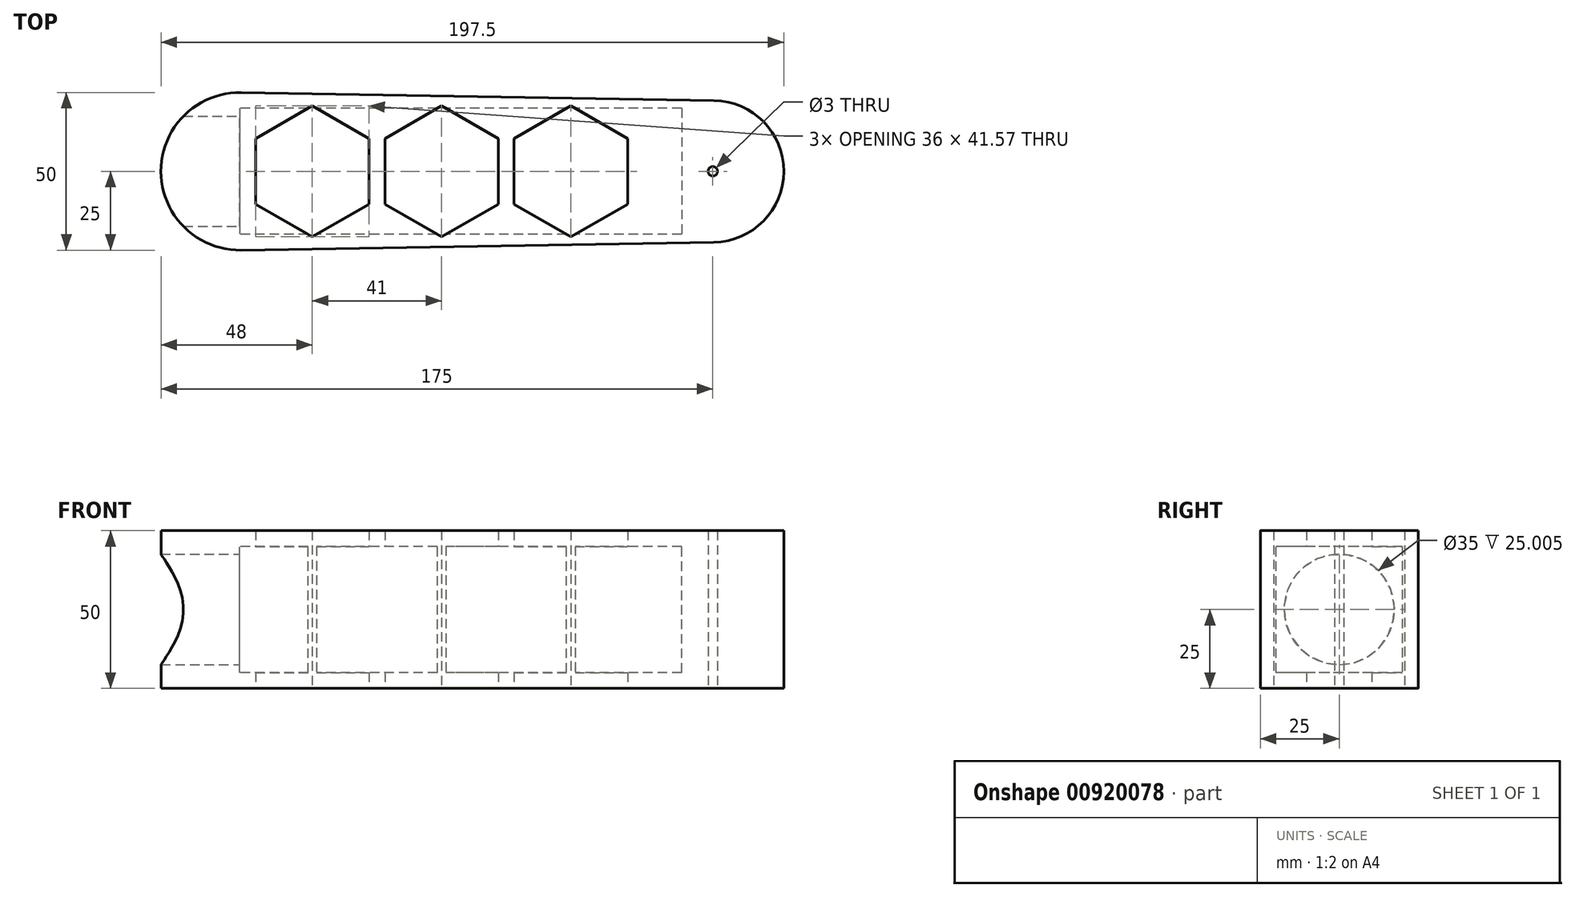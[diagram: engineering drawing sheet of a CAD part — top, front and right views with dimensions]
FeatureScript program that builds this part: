
annotation { "Feature Type Name" : "Feature", "Feature Type Description" : "" }
export const myFeature = defineFeature(function(context is Context, id is Id, definition is map)
    precondition{}
    {
        {
            var Q0;
            Q0=qCreatedBy(makeId("Top.planeOp"),FACE);
            var sketch = newSketch(context, id + "F0", { "sketchPlane" : qUnion([Q0])});
            skCircle(sketch, "E0", {"center": v(150, 0) * mm, "radius": 1.5 * mm});
            skLineSegment(sketch, "E1", {"start": v(0, 0) * mm, "end": v(150, 0) * mm, "construction": true});
            skArc(sketch, "E2", {"start": v(0.42, 25) * mm, "mid": v(-25, 0) * mm, "end": v(0.42, -25) * mm});
            skLineSegment(sketch, "E3", {"start": v(0.42, 25) * mm, "end": v(150.37, 22.5) * mm});
            skLineSegment(sketch, "E4", {"start": v(150.37, -22.5) * mm, "end": v(0.42, -25) * mm});
            skArc(sketch, "E5", {"start": v(150.37, 22.5) * mm, "mid": v(127.5, 0) * mm, "end": v(150.37, -22.5) * mm, "construction": true});
            skArc(sketch, "E6", {"start": v(150.37, -22.5) * mm, "mid": v(172.5, 0) * mm, "end": v(150.37, 22.5) * mm});
            skSolve(sketch);
        }
        {
            var Q0;
            Q0=makeQuery(id+"F0.imprint","IMPRINT",FACE,{"disambiguationData":[TD([[makeQuery(id+"F0.imprint","IMPRINT",EDGE,{"derivedFrom":sQuery(id+"F0.wireOp",EDGE,"E0")}),-1.0]])]});
            var sketch = newSketch(context, id + "F1", { "sketchPlane" : qUnion([Q0])});
            skCircle(sketch, "E7.cCircle", {"center": v(23, 0) * mm, "radius": 18 * mm, "construction": true});
            skLineSegment(sketch, "E7.0", {"start": v(5, -10.4) * mm, "end": v(5, 10.4) * mm});
            skLineSegment(sketch, "E7.1", {"start": v(5, 10.4) * mm, "end": v(23, 20.78) * mm});
            skLineSegment(sketch, "E7.2", {"start": v(23, 20.78) * mm, "end": v(41, 10.4) * mm});
            skLineSegment(sketch, "E7.3", {"start": v(41, 10.4) * mm, "end": v(41, -10.4) * mm});
            skLineSegment(sketch, "E7.4", {"start": v(41, -10.4) * mm, "end": v(23, -20.78) * mm});
            skLineSegment(sketch, "E7.5", {"start": v(23, -20.78) * mm, "end": v(5, -10.4) * mm});
            skPoint(sketch, "E7.0.midPoint", {"position": v(5, 0) * mm});
            skCircle(sketch, "E8.cCircle", {"center": v(64, 0) * mm, "radius": 18 * mm, "construction": true});
            skLineSegment(sketch, "E8.0", {"start": v(82, 10.4) * mm, "end": v(82, -10.4) * mm});
            skLineSegment(sketch, "E8.1", {"start": v(82, -10.4) * mm, "end": v(64, -20.78) * mm});
            skLineSegment(sketch, "E8.2", {"start": v(64, -20.78) * mm, "end": v(46, -10.4) * mm});
            skLineSegment(sketch, "E8.3", {"start": v(46, -10.4) * mm, "end": v(46, 10.4) * mm});
            skLineSegment(sketch, "E8.4", {"start": v(46, 10.4) * mm, "end": v(64, 20.78) * mm});
            skLineSegment(sketch, "E8.5", {"start": v(64, 20.78) * mm, "end": v(82, 10.4) * mm});
            skPoint(sketch, "E8.0.midPoint", {"position": v(82, 0) * mm});
            skCircle(sketch, "E9.cCircle", {"center": v(105, 0) * mm, "radius": 18 * mm, "construction": true});
            skLineSegment(sketch, "E9.0", {"start": v(87, -10.4) * mm, "end": v(87, 10.4) * mm});
            skLineSegment(sketch, "E9.1", {"start": v(87, 10.4) * mm, "end": v(105, 20.78) * mm});
            skLineSegment(sketch, "E9.2", {"start": v(105, 20.78) * mm, "end": v(123, 10.4) * mm});
            skLineSegment(sketch, "E9.3", {"start": v(123, 10.4) * mm, "end": v(123, -10.4) * mm});
            skLineSegment(sketch, "E9.4", {"start": v(123, -10.4) * mm, "end": v(105, -20.78) * mm});
            skLineSegment(sketch, "E9.5", {"start": v(105, -20.78) * mm, "end": v(87, -10.4) * mm});
            skPoint(sketch, "E9.0.midPoint", {"position": v(87, 0) * mm});
            skSolve(sketch);
        }
        {
            var Q0;
            Q0=makeQuery(id+"F0.imprint","IMPRINT",FACE,{"disambiguationData":[TD([[makeQuery(id+"F0.imprint","IMPRINT",EDGE,{"derivedFrom":sQuery(id+"F0.wireOp",EDGE,"E0")}),-1.0]])]});
            extrude(context, id + "F2", {"entities" : qUnion([Q0]), "depth" : 50 * mm, "offsetDistance" : 25 * mm});
        }
        {
            var Q0;
            Q0 = qSketchRegion(id + "F1", true);
            extrude(context, id + "F3", {"entities" : qUnion([Q0]), "operationType" : NewBodyOperationType.REMOVE, "depth" : 60 * mm, "offsetDistance" : 25 * mm});
        }
        {
            var Q0;
            Q0=qCreatedBy(makeId("Right.planeOp"),FACE);
            var sketch = newSketch(context, id + "F4", { "sketchPlane" : qUnion([Q0])});
            skLineSegment(sketch, "E10.bottom", {"start": v(25, 0) * mm, "end": v(-25, 0) * mm, "construction": true});
            skLineSegment(sketch, "E10.top", {"start": v(25, 50) * mm, "end": v(-25, 50) * mm, "construction": true});
            skLineSegment(sketch, "E10.left", {"start": v(25, 0) * mm, "end": v(25, 50) * mm, "construction": true});
            skLineSegment(sketch, "E10.right", {"start": v(-25, 0) * mm, "end": v(-25, 50) * mm, "construction": true});
            skLineSegment(sketch, "E11.0", {"start": v(20, 5) * mm, "end": v(-20, 5) * mm});
            skLineSegment(sketch, "E11.1", {"start": v(20, 5) * mm, "end": v(20, 45) * mm});
            skLineSegment(sketch, "E11.2", {"start": v(20, 45) * mm, "end": v(-20, 45) * mm});
            skLineSegment(sketch, "E11.3", {"start": v(-20, 5) * mm, "end": v(-20, 45) * mm});
            skSolve(sketch);
        }
        {
            var Q0;
            Q0 = qSketchRegion(id + "F4", true);
            extrude(context, id + "F5", {"entities" : qUnion([Q0]), "operationType" : NewBodyOperationType.REMOVE, "depth" : 140.1 * mm, "offsetDistance" : 25 * mm});
        }
        {
            var Q0;
            Q0=qCreatedBy(makeId("Right.planeOp"),FACE);
            var sketch = newSketch(context, id + "F6", { "sketchPlane" : qUnion([Q0])});
            skCircle(sketch, "E12", {"center": v(0, 25) * mm, "radius": 17.5 * mm});
            skSolve(sketch);
        }
        {
            var Q0;
            Q0 = qSketchRegion(id + "F6", true);
            extrude(context, id + "F7", {"entities" : qUnion([Q0]), "operationType" : NewBodyOperationType.REMOVE, "endBound" : BoundingType.THROUGH_ALL, "oppositeDirection" : true, "depth" : 25 * mm, "offsetDistance" : 25 * mm});
        }
    });
